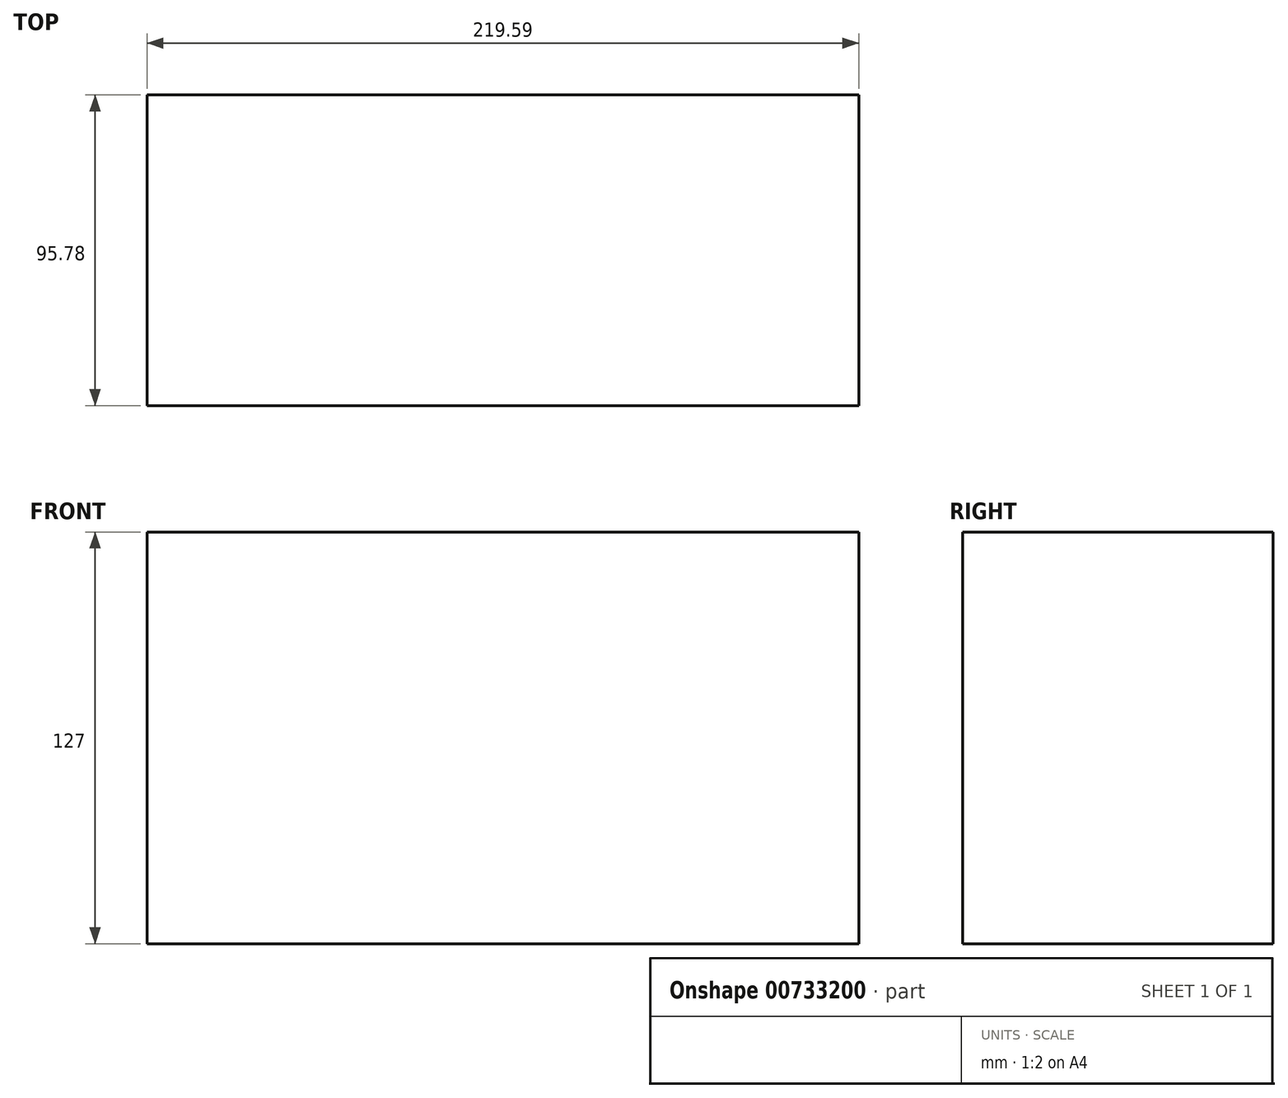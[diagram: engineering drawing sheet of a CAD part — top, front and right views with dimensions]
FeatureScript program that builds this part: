
annotation { "Feature Type Name" : "Feature", "Feature Type Description" : "" }
export const myFeature = defineFeature(function(context is Context, id is Id, definition is map)
    precondition{}
    {
        {
            var Q0;
            Q0=qCreatedBy(makeId("Top.planeOp"),FACE);
            var sketch = newSketch(context, id + "F0", { "sketchPlane" : qUnion([Q0])});
            skLineSegment(sketch, "E0.bottom", {"start": v(-75.78, 63.22) * mm, "end": v(143.81, 63.22) * mm});
            skLineSegment(sketch, "E0.top", {"start": v(-75.78, -32.56) * mm, "end": v(143.81, -32.56) * mm});
            skLineSegment(sketch, "E0.left", {"start": v(-75.78, 63.22) * mm, "end": v(-75.78, -32.56) * mm});
            skLineSegment(sketch, "E0.right", {"start": v(143.81, 63.22) * mm, "end": v(143.81, -32.56) * mm});
            skSolve(sketch);
        }
        {
            var Q0;
            Q0 = qSketchRegion(id + "F0", true);
            extrude(context, id + "F1", {"entities" : qUnion([Q0]), "depth" : 127 * mm, "offsetDistance" : 25.4 * mm});
        }
        {
            var Q0;
            Q0=makeQuery(id+"F1.opExtrude","CAP_FACE",FACE,{"disambiguationData":[OSD([sQuery(id+"F0.wireOp",EDGE,"E0.bottom"),sQuery(id+"F0.wireOp",EDGE,"E0.top"),sQuery(id+"F0.wireOp",EDGE,"E0.left"),sQuery(id+"F0.wireOp",EDGE,"E0.right")])],"isStart":false});
            var sketch = newSketch(context, id + "F2", { "sketchPlane" : qUnion([Q0])});
            skCircle(sketch, "E1", {"center": v(-70.27, 50.38) * mm, "radius": 3.72 * mm});
            skCircle(sketch, "E2", {"center": v(-59.13, 43.07) * mm, "radius": 3.72 * mm});
            skCircle(sketch, "E3", {"center": v(-55.04, 55.92) * mm, "radius": 3.72 * mm});
            skCircle(sketch, "E4", {"center": v(-13.87, 58.55) * mm, "radius": 3.72 * mm});
            skCircle(sketch, "E5", {"center": v(-9.5, 50.08) * mm, "radius": 3.72 * mm});
            skCircle(sketch, "E6", {"center": v(2.48, 56.5) * mm, "radius": 3.72 * mm});
            skCircle(sketch, "E7", {"center": v(37.23, 59.13) * mm, "radius": 3.72 * mm});
            skCircle(sketch, "E8", {"center": v(45.12, 46.58) * mm, "radius": 3.72 * mm});
            skCircle(sketch, "E9", {"center": v(52.7, 58.26) * mm, "radius": 3.72 * mm});
            skCircle(sketch, "E10", {"center": v(97.97, 60) * mm, "radius": 3.72 * mm});
            skCircle(sketch, "E11", {"center": v(103.52, 46.57) * mm, "radius": 3.72 * mm});
            skCircle(sketch, "E12", {"center": v(111.99, 56.22) * mm, "radius": 3.72 * mm});
            skCircle(sketch, "E13", {"center": v(-67.61, -1.73) * mm, "radius": 3.72 * mm});
            skCircle(sketch, "E14", {"center": v(-63.52, -16.05) * mm, "radius": 3.72 * mm});
            skCircle(sketch, "E15", {"center": v(-50.1, -6.1) * mm, "radius": 3.72 * mm});
            skCircle(sketch, "E16", {"center": v(-12.47, -1.98) * mm, "radius": 3.72 * mm});
            skCircle(sketch, "E17", {"center": v(-8.08, -15.42) * mm, "radius": 3.72 * mm});
            skCircle(sketch, "E18", {"center": v(3.88, -6.36) * mm, "radius": 3.72 * mm});
            skCircle(sketch, "E19", {"center": v(37.75, -0.2) * mm, "radius": 3.72 * mm});
            skCircle(sketch, "E20", {"center": v(40.4, -17.74) * mm, "radius": 3.72 * mm});
            skCircle(sketch, "E21", {"center": v(52.36, -9.55) * mm, "radius": 3.72 * mm});
            skCircle(sketch, "E22", {"center": v(93.87, -0.48) * mm, "radius": 3.72 * mm});
            skCircle(sketch, "E23", {"center": v(103.81, -5.73) * mm, "radius": 3.72 * mm});
            skCircle(sketch, "E24", {"center": v(99.15, -14.79) * mm, "radius": 3.72 * mm});
            skSolve(sketch);
        }
        {
            var Q0;
            Q0=sQuery(id+"F2.wireOp",EDGE,"E8");
            var Q1;
            Q1=sQuery(id+"F2.wireOp",EDGE,"E11");
            var Q2;
            Q2=sQuery(id+"F2.wireOp",EDGE,"E6");
            var Q3;
            Q3=sQuery(id+"F2.wireOp",EDGE,"E4");
            var Q4;
            Q4=sQuery(id+"F2.wireOp",EDGE,"E18");
            var Q5;
            Q5=sQuery(id+"F2.wireOp",EDGE,"E19");
            var Q6;
            Q6=sQuery(id+"F2.wireOp",EDGE,"E17");
            var Q7;
            Q7=sQuery(id+"F2.wireOp",EDGE,"E2");
            var Q8;
            Q8=sQuery(id+"F2.wireOp",EDGE,"E16");
            var Q9;
            Q9=sQuery(id+"F2.wireOp",EDGE,"E24");
            var Q10;
            Q10=sQuery(id+"F2.wireOp",EDGE,"E15");
            var Q11;
            Q11=sQuery(id+"F2.wireOp",EDGE,"E21");
            var Q12;
            Q12=sQuery(id+"F2.wireOp",EDGE,"E23");
            var Q13;
            Q13=sQuery(id+"F2.wireOp",EDGE,"E22");
            var Q14;
            Q14=sQuery(id+"F2.wireOp",EDGE,"E5");
            var Q15;
            Q15=sQuery(id+"F2.wireOp",EDGE,"E9");
            var Q16;
            Q16=sQuery(id+"F2.wireOp",EDGE,"E10");
            var Q17;
            Q17=sQuery(id+"F2.wireOp",EDGE,"E20");
            var Q18;
            Q18=sQuery(id+"F2.wireOp",EDGE,"E7");
            var Q19;
            Q19=sQuery(id+"F2.wireOp",EDGE,"E12");
            var Q20;
            Q20=sQuery(id+"F2.wireOp",EDGE,"E14");
            var Q21;
            Q21=sQuery(id+"F2.wireOp",EDGE,"E13");
            var Q22;
            Q22=sQuery(id+"F2.wireOp",EDGE,"E3");
            var Q23;
            Q23=sQuery(id+"F2.wireOp",EDGE,"E1");
            extrude(context, id + "F3", {"bodyType" : ToolBodyType.SURFACE, "surfaceEntities" : qUnion([Q0, Q1, Q2, Q3, Q4, Q5, Q6, Q7, Q8, Q9, Q10, Q11, Q12, Q13, Q14, Q15, Q16, Q17, Q18, Q19, Q20, Q21, Q22, Q23]), "oppositeDirection" : true, "depth" : 50.8 * mm, "offsetDistance" : 25.4 * mm});
        }
    });
